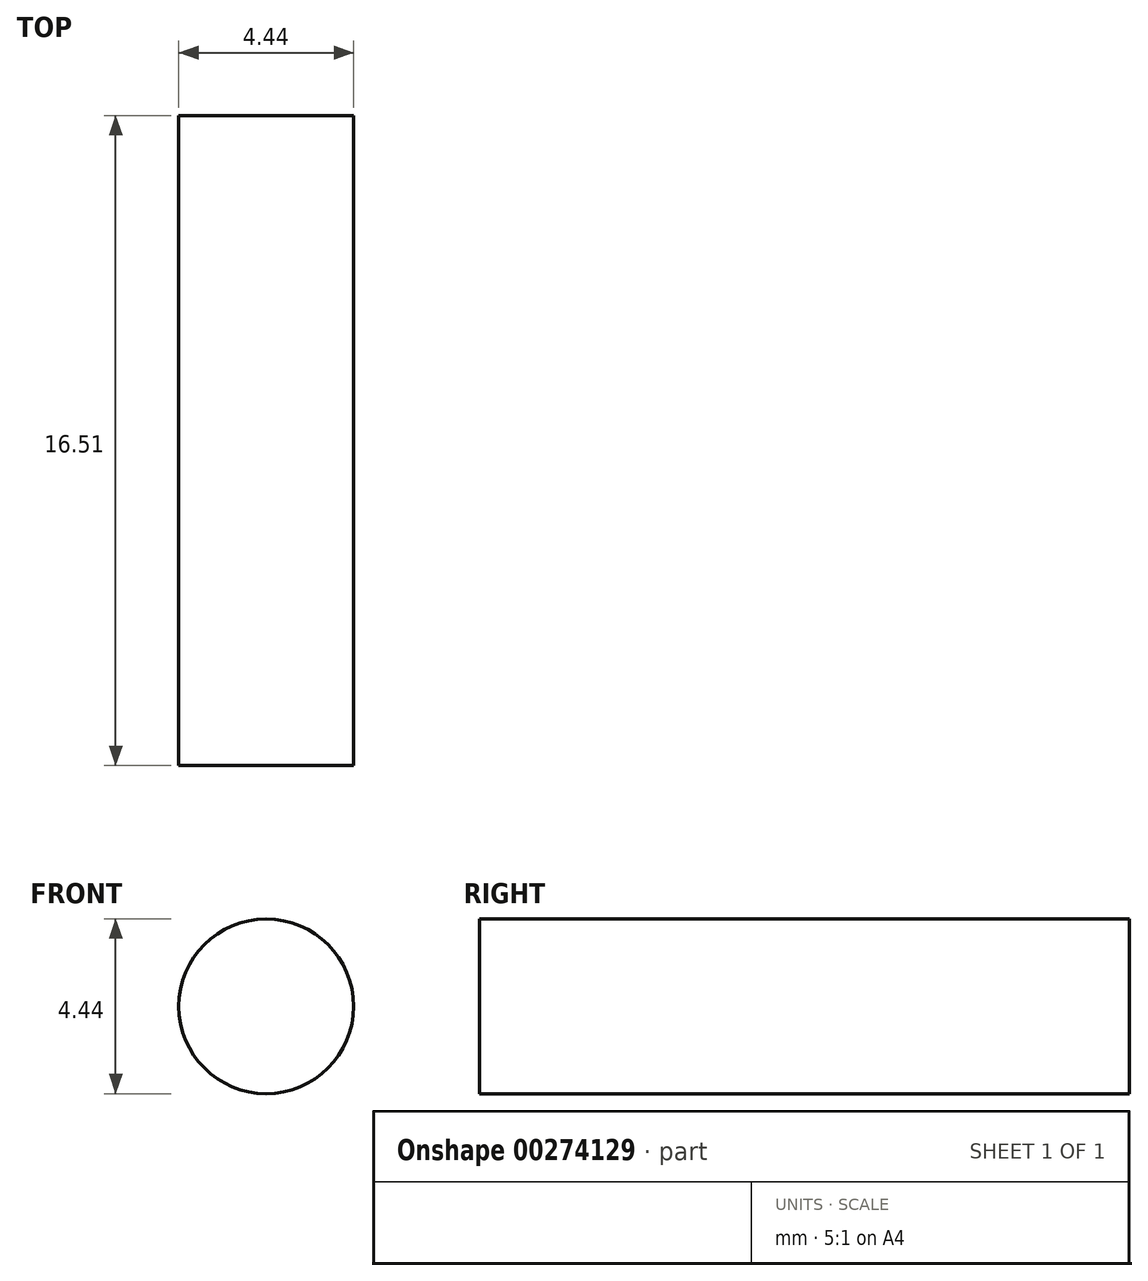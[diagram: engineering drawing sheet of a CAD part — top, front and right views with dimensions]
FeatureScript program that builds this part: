
annotation { "Feature Type Name" : "Feature", "Feature Type Description" : "" }
export const myFeature = defineFeature(function(context is Context, id is Id, definition is map)
    precondition{}
    {
        {
            var Q0;
            Q0=qCreatedBy(makeId("Front.planeOp"),FACE);
            var sketch = newSketch(context, id + "F0", { "sketchPlane" : qUnion([Q0])});
            skCircle(sketch, "E0", {"center": v(0, 0) * mm, "radius": 2.22 * mm});
            skSolve(sketch);
        }
        {
            var Q0;
            Q0=makeQuery(id+"F0.imprint","IMPRINT",FACE,{"disambiguationData":[TD([[makeQuery(id+"F0.imprint","IMPRINT",EDGE,{"derivedFrom":sQuery(id+"F0.wireOp",EDGE,"E0")}),1.0]])]});
            extrude(context, id + "F1", {"entities" : qUnion([Q0]), "depth" : 16.5 * mm});
        }
    });
